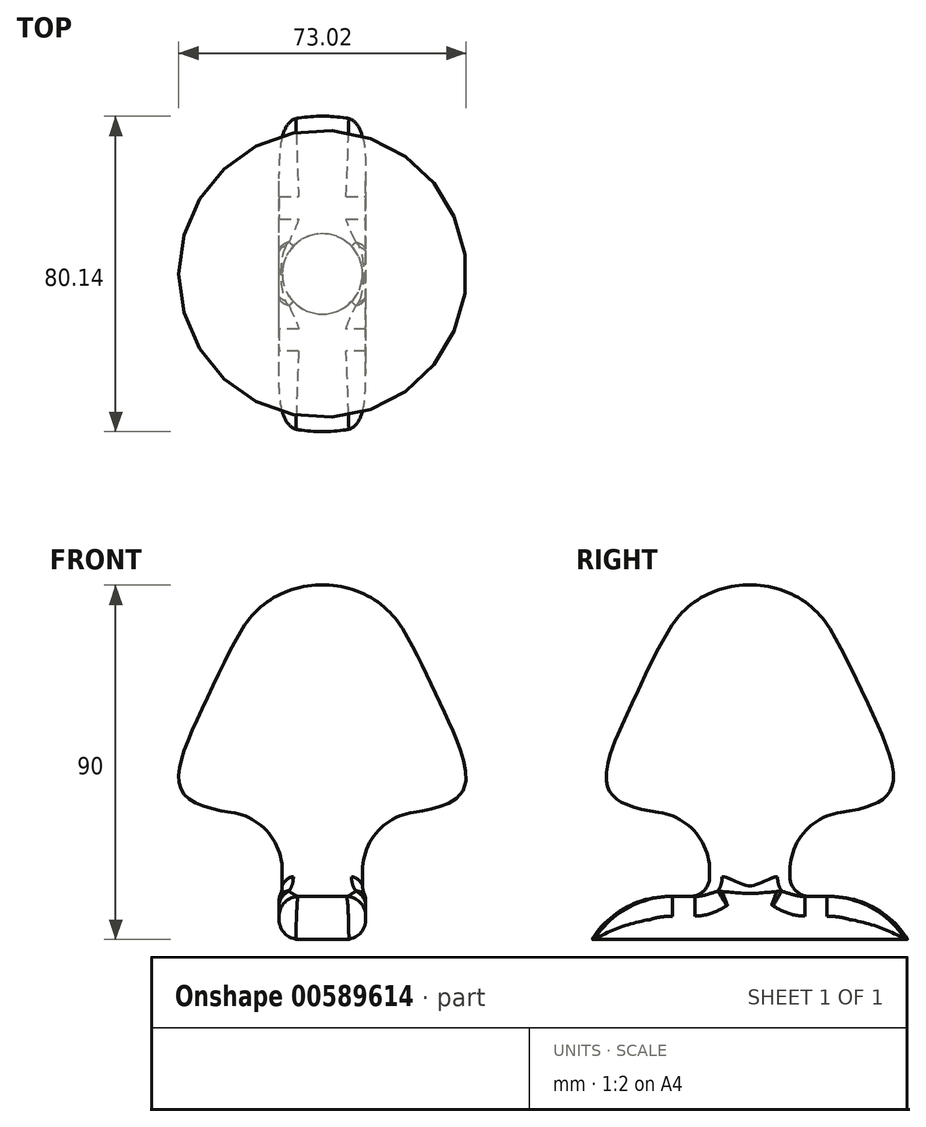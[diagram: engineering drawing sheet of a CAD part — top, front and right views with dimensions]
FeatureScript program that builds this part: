
annotation { "Feature Type Name" : "Feature", "Feature Type Description" : "" }
export const myFeature = defineFeature(function(context is Context, id is Id, definition is map)
    precondition{}
    {
        {
            var Q0;
            Q0=qCreatedBy(makeId("Front.planeOp"),FACE);
            var sketch = newSketch(context, id + "F0", { "sketchPlane" : qUnion([Q0])});
            skLineSegment(sketch, "E0", {"start": v(0, 0) * mm, "end": v(0, 90) * mm});
            skLineSegment(sketch, "E1", {"start": v(0, 0) * mm, "end": v(40.07, 0) * mm});
            skLineSegment(sketch, "E2", {"start": v(40.07, 0) * mm, "end": v(40.07, 10.9) * mm});
            skLineSegment(sketch, "E3", {"start": v(40.07, 10.9) * mm, "end": v(10.2, 10.9) * mm});
            skLineSegment(sketch, "E4", {"start": v(10.2, 10.9) * mm, "end": v(10.2, 31.23) * mm});
            skLineSegment(sketch, "E5", {"start": v(0, 90) * mm, "end": v(9.2, 90) * mm});
            skFitSpline(sketch, "E6", {"points": [v(9.2, 90) * mm, v(30, 59.8) * mm, v(35, 36.7) * mm, v(10.2, 31.23) * mm], "startDerivative": vector(61.84, -15.36) * mm, "endDerivative": vector(-80.07, -5.08) * mm});
            skLineSegment(sketch, "E7", {"start": v(35, 36.7) * mm, "end": v(0, 36.7) * mm, "construction": true});
            skLineSegment(sketch, "E8", {"start": v(30, 59.8) * mm, "end": v(0, 59.8) * mm, "construction": true});
            skSolve(sketch);
        }
        {
            var Q0;
            Q0=makeQuery(id+"F0.imprint","IMPRINT",FACE,{"disambiguationData":[TD([[makeQuery(id+"F0.imprint","IMPRINT",EDGE,{"derivedFrom":sQuery(id+"F0.wireOp",EDGE,"E0")}),-1.0]])]});
            var Q1;
            Q1=sQuery(id+"F0.wireOp",EDGE,"E0");
            revolve(context, id + "F1", {"entities" : qUnion([Q0]), "axis" : qUnion([Q1]), "revolveType" : RevolveType.FULL});
        }
        {
            var Q0;
            Q0=makeQuery(id+"F1.opRevolve","SWEPT_EDGE",EDGE,{"disambiguationData":[OSD([sQuery(id+"F0.wireOp",EDGE,"E5"),sQuery(id+"F0.wireOp",EDGE,"E6")])]});
            var Q1;
            Q1=makeQuery(id+"F1.opRevolve","SWEPT_EDGE",EDGE,{"disambiguationData":[OSD([sQuery(id+"F0.wireOp",EDGE,"E2"),sQuery(id+"F0.wireOp",EDGE,"E3")])]});
            fillet(context, id + "F2", {"entities" : qUnion([Q0, Q1]), "radius" : 23 * mm, "tangentPropagation" : true, "allowEdgeOverflow" : false});
        }
        {
            var Q0;
            Q0=makeQuery(id+"F1.opRevolve","SWEPT_FACE",FACE,{"disambiguationData":[OSD([sQuery(id+"F0.wireOp",EDGE,"E1")])]});
            var sketch = newSketch(context, id + "F3", { "sketchPlane" : qUnion([Q0])});
            skLineSegment(sketch, "E9.bottom", {"start": v(-11, 50) * mm, "end": v(11, 50) * mm});
            skLineSegment(sketch, "E9.top", {"start": v(-11, -50) * mm, "end": v(11, -50) * mm});
            skLineSegment(sketch, "E9.left", {"start": v(-11, 50) * mm, "end": v(-11, -50) * mm});
            skLineSegment(sketch, "E9.right", {"start": v(11, 50) * mm, "end": v(11, -50) * mm});
            skLineSegment(sketch, "E10.0", {"start": v(47.42, 86.42) * mm, "end": v(47.42, -86.42) * mm});
            skLineSegment(sketch, "E10.1", {"start": v(-47.42, 86.42) * mm, "end": v(47.42, 86.42) * mm});
            skLineSegment(sketch, "E10.2", {"start": v(-47.42, 86.42) * mm, "end": v(-47.42, -86.42) * mm});
            skLineSegment(sketch, "E10.3", {"start": v(-47.42, -86.42) * mm, "end": v(47.42, -86.42) * mm});
            skSolve(sketch);
        }
        {
            var Q0;
            {var subQ0=sQuery(id+"F3.wireOp",EDGE,"E9.right");var subQ1=makeQuery(id+"F2.opFillet","BLEND_EDGE",EDGE,{"blendedFrom":[makeQuery(id+"F1.opRevolve","SWEPT_EDGE",EDGE,{"disambiguationData":[OSD([sQuery(id+"F0.wireOp",EDGE,"E2"),sQuery(id+"F0.wireOp",EDGE,"E3")])]}),makeQuery(id+"F1.opRevolve","SWEPT_FACE",FACE,{"disambiguationData":[OSD([sQuery(id+"F0.wireOp",EDGE,"E1")])]})],"blendedInto":[makeQuery(id+"F1.opRevolve","SWEPT_FACE",FACE,{"disambiguationData":[OSD([sQuery(id+"F0.wireOp",EDGE,"E1")])]})]});var subQ2=makeQuery(id+"F3.imprint","INTERSECT",VERTEX,{"disambiguationData":[OD(0.0)],"derivedFrom":[subQ1,subQ0]});Q0=makeQuery(id+"F3.imprint","IMPRINT",FACE,{"disambiguationData":[TD([[makeQuery(id+"F3.imprint","IMPRINT",EDGE,{"disambiguationData":[TD([[subQ2,-1.0]])],"derivedFrom":subQ0}),1.0]])]});}
            var Q1;
            {var subQ0=sQuery(id+"F3.wireOp",EDGE,"E9.left");var subQ1=makeQuery(id+"F2.opFillet","BLEND_EDGE",EDGE,{"blendedFrom":[makeQuery(id+"F1.opRevolve","SWEPT_EDGE",EDGE,{"disambiguationData":[OSD([sQuery(id+"F0.wireOp",EDGE,"E2"),sQuery(id+"F0.wireOp",EDGE,"E3")])]}),makeQuery(id+"F1.opRevolve","SWEPT_FACE",FACE,{"disambiguationData":[OSD([sQuery(id+"F0.wireOp",EDGE,"E1")])]})],"blendedInto":[makeQuery(id+"F1.opRevolve","SWEPT_FACE",FACE,{"disambiguationData":[OSD([sQuery(id+"F0.wireOp",EDGE,"E1")])]})]});var subQ2=makeQuery(id+"F3.imprint","INTERSECT",VERTEX,{"disambiguationData":[OD(0.0)],"derivedFrom":[subQ1,subQ0]});Q1=makeQuery(id+"F3.imprint","IMPRINT",FACE,{"disambiguationData":[TD([[makeQuery(id+"F3.imprint","IMPRINT",EDGE,{"disambiguationData":[TD([[subQ2,-1.0]])],"derivedFrom":subQ0}),-1.0]])]});}
            extrude(context, id + "F4", {"entities" : qUnion([Q0, Q1]), "operationType" : NewBodyOperationType.REMOVE, "oppositeDirection" : true, "depth" : 17.7 * mm, "offsetDistance" : 25 * mm});
        }
        {
            var Q0;
            Q0=makeQuery(id+"F1.opRevolve","SWEPT_EDGE",EDGE,{"disambiguationData":[OSD([sQuery(id+"F0.wireOp",EDGE,"E3"),sQuery(id+"F0.wireOp",EDGE,"E4")])]});
            fillet(context, id + "F5", {"entities" : qUnion([Q0]), "radius" : 5 * mm, "tangentPropagation" : true, "allowEdgeOverflow" : false});
        }
        {
            var Q0;
            Q0=makeQuery(id+"F4.boolean.opBoolean","COPY",FACE,{"derivedFrom":makeQuery(id+"F4.opExtrude","SWEPT_FACE",FACE,{"disambiguationData":[OSD([sQuery(id+"F3.wireOp",EDGE,"E9.right")])]})});
            var Q1;
            Q1=makeQuery(id+"F4.boolean.opBoolean","COPY",FACE,{"derivedFrom":makeQuery(id+"F4.opExtrude","SWEPT_FACE",FACE,{"disambiguationData":[OSD([sQuery(id+"F3.wireOp",EDGE,"E9.left")])]})});
            fillet(context, id + "F6", {"entities" : qUnion([Q0, Q1]), "radius" : 5 * mm, "tangentPropagation" : true, "allowEdgeOverflow" : false});
        }
        {
            var Q0;
            Q0=makeQuery(id+"F1.opRevolve","SWEPT_EDGE",EDGE,{"disambiguationData":[OSD([sQuery(id+"F0.wireOp",EDGE,"E4"),sQuery(id+"F0.wireOp",EDGE,"E6")])]});
            fillet(context, id + "F7", {"entities" : qUnion([Q0]), "radius" : 15 * mm, "tangentPropagation" : true, "allowEdgeOverflow" : false});
        }
    });
